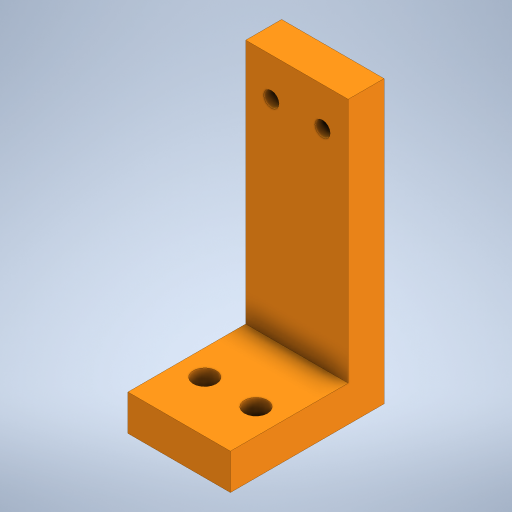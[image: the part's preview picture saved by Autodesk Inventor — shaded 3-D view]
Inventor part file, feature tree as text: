
AUTODESK INVENTOR PART (.ipt)
format: ipt  version: 2023 (Build 270158000, 158)  size: 248,320 bytes
history: native  units: mm
features: extrude x2, sketch x2
ambient origin geometry x8: Origin, YZ Plane, XZ Plane, XY Plane, X Axis, Y Axis, Z Axis, Center Point
bodies: Solid1 (feature_tree)
feature tree (4):
  extrude  "Extrusion1"  Depth=3.0mm
  extrude  "Extrusion2"  Depth=20.0mm
  sketch  "Sketch1"  dims[d0=3.0mm d1=3.0mm]
  sketch  "Sketch2"  dims[d2=10.0mm d3=20.0mm d4=7.5mm d5=7.5mm d6=5.0mm d7=55.0mm d8=7.0mm d9=0.0mm d10=30.0mm d11=4.5mm d12=4.5mm d13=10.0mm d14=5.0mm d15=10.0mm d16=7.0mm d17=0.0mm]
